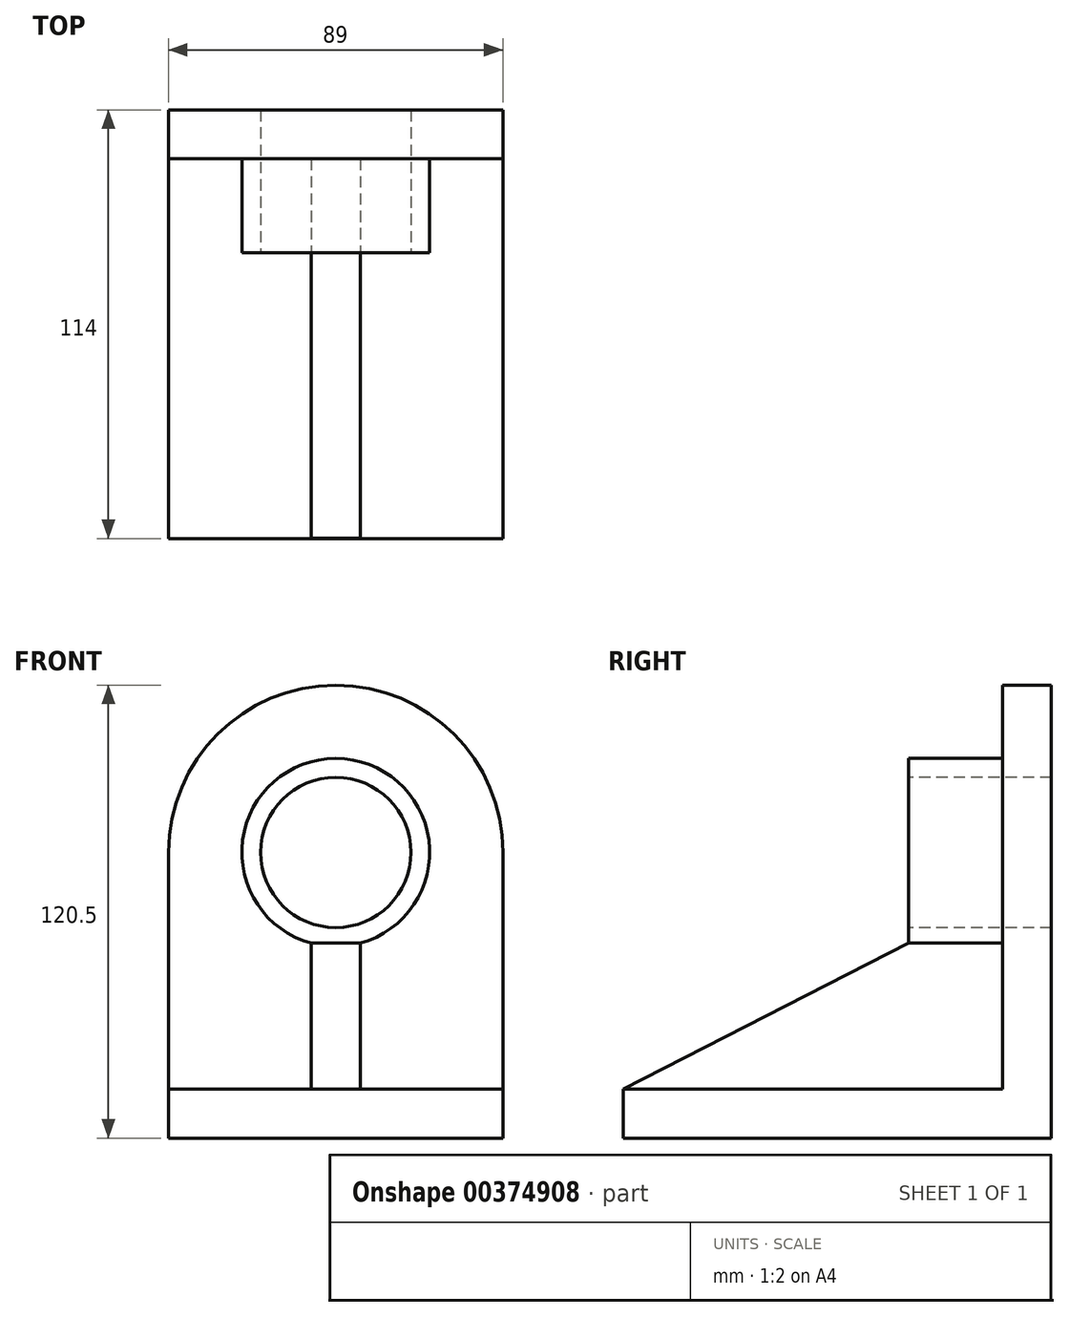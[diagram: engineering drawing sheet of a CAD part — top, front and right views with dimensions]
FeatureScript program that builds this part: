
annotation { "Feature Type Name" : "Feature", "Feature Type Description" : "" }
export const myFeature = defineFeature(function(context is Context, id is Id, definition is map)
    precondition{}
    {
        {
            var Q0;
            Q0=qCreatedBy(makeId("Right.planeOp"),FACE);
            var sketch = newSketch(context, id + "F0", { "sketchPlane" : qUnion([Q0])});
            skLineSegment(sketch, "E0", {"start": v(-64.11, -63.37) * mm, "end": v(49.89, -63.37) * mm});
            skLineSegment(sketch, "E1", {"start": v(49.89, -63.37) * mm, "end": v(49.89, 57.13) * mm});
            skLineSegment(sketch, "E2", {"start": v(49.89, 57.13) * mm, "end": v(36.89, 57.13) * mm});
            skLineSegment(sketch, "E3", {"start": v(36.89, 57.13) * mm, "end": v(36.89, -50.37) * mm});
            skLineSegment(sketch, "E4", {"start": v(36.89, -50.37) * mm, "end": v(-64.11, -50.37) * mm});
            skLineSegment(sketch, "E5", {"start": v(-64.11, -63.37) * mm, "end": v(-64.11, -50.37) * mm});
            skSolve(sketch);
        }
        {
            var Q0;
            Q0=makeQuery(id+"F0.imprint","IMPRINT",FACE,{"disambiguationData":[TD([[makeQuery(id+"F0.imprint","IMPRINT",EDGE,{"derivedFrom":sQuery(id+"F0.wireOp",EDGE,"E0")}),1.0]])]});
            extrude(context, id + "F1", {"entities" : qUnion([Q0]), "depth" : 44.5 * mm, "hasSecondDirection" : true, "secondDirectionOppositeDirection" : true, "secondDirectionDepth" : 44.5 * mm});
        }
        {
            var Q0;
            Q0=makeQuery(id+"F1.opExtrude","SWEPT_FACE",FACE,{"disambiguationData":[OSD([sQuery(id+"F0.wireOp",EDGE,"E3")])]});
            var sketch = newSketch(context, id + "F2", { "sketchPlane" : qUnion([Q0])});
            skArc(sketch, "E6", {"start": v(44.5, 12.63) * mm, "mid": v(0, 57.13) * mm, "end": v(-44.5, 12.63) * mm});
            skLineSegment(sketch, "E7", {"start": v(-44.5, 12.63) * mm, "end": v(-44.5, 57.13) * mm});
            skLineSegment(sketch, "E8", {"start": v(-44.5, 57.13) * mm, "end": v(44.5, 57.13) * mm});
            skLineSegment(sketch, "E9", {"start": v(44.5, 57.13) * mm, "end": v(44.5, 12.63) * mm});
            skCircle(sketch, "E10", {"center": v(0, 12.63) * mm, "radius": 20 * mm});
            skCircle(sketch, "E11.0", {"center": v(0, 12.63) * mm, "radius": 25 * mm});
            skSolve(sketch);
        }
        {
            var Q0;
            {var subQ0=sQuery(id+"F2.wireOp",EDGE,"E9");Q0=makeQuery(id+"F2.imprint","IMPRINT",FACE,{"disambiguationData":[TD([[makeQuery(id+"F2.imprint","IMPRINT",EDGE,{"derivedFrom":subQ0}),-1.0]])]});}
            var Q1;
            {var subQ0=sQuery(id+"F2.wireOp",EDGE,"E7");Q1=makeQuery(id+"F2.imprint","IMPRINT",FACE,{"disambiguationData":[TD([[makeQuery(id+"F2.imprint","IMPRINT",EDGE,{"derivedFrom":subQ0}),1.0]])]});}
            extrude(context, id + "F3", {"entities" : qUnion([Q0, Q1]), "operationType" : NewBodyOperationType.REMOVE, "oppositeDirection" : true, "depth" : 25.4 * mm});
        }
        {
            var Q0;
            Q0=makeQuery(id+"F2.imprint","IMPRINT",FACE,{"disambiguationData":[TD([[makeQuery(id+"F2.imprint","IMPRINT",EDGE,{"derivedFrom":sQuery(id+"F2.wireOp",EDGE,"E10")}),1.0]])]});
            extrude(context, id + "F4", {"entities" : qUnion([Q0]), "operationType" : NewBodyOperationType.REMOVE, "oppositeDirection" : true, "depth" : 25.4 * mm});
        }
        {
            var Q0;
            Q0=makeQuery(id+"F2.imprint","IMPRINT",FACE,{"disambiguationData":[TD([[makeQuery(id+"F2.imprint","IMPRINT",EDGE,{"derivedFrom":sQuery(id+"F2.wireOp",EDGE,"E10")}),-1.0]])]});
            extrude(context, id + "F5", {"entities" : qUnion([Q0]), "operationType" : NewBodyOperationType.ADD, "depth" : 25 * mm});
        }
        {
            var Q0;
            Q0=makeQuery(id+"F5.opExtrude","CAP_FACE",FACE,{"disambiguationData":[OSD([sQuery(id+"F2.wireOp",EDGE,"E10"),sQuery(id+"F2.wireOp",EDGE,"E11.0")])],"isStart":false});
            var sketch = newSketch(context, id + "F6", { "sketchPlane" : qUnion([Q0])});
            skLineSegment(sketch, "E12", {"start": v(0, -7.37) * mm, "end": v(6.5, -7.37) * mm});
            skLineSegment(sketch, "E13", {"start": v(6.5, -7.37) * mm, "end": v(6.5, -50.55) * mm});
            skLineSegment(sketch, "E14", {"start": v(6.5, -50.55) * mm, "end": v(0, -50.55) * mm});
            skLineSegment(sketch, "E15.MirrorCS", {"start": v(0, -7.37) * mm, "end": v(-6.5, -7.37) * mm});
            skLineSegment(sketch, "E16.MirrorCS", {"start": v(-6.5, -7.37) * mm, "end": v(-6.5, -50.55) * mm});
            skLineSegment(sketch, "E17.MirrorCS", {"start": v(-6.5, -50.55) * mm, "end": v(0, -50.55) * mm});
            skSolve(sketch);
        }
        {
            var Q0;
            {var subQ4=sQuery(id+"F6.wireOp",EDGE,"E14");Q0=makeQuery(id+"F6.imprint","IMPRINT",FACE,{"disambiguationData":[TD([[makeQuery(id+"F6.imprint","IMPRINT",EDGE,{"derivedFrom":subQ4}),-1.0]])]});}
            extrude(context, id + "F7", {"entities" : qUnion([Q0]), "operationType" : NewBodyOperationType.ADD, "endBound" : BoundingType.UP_TO_NEXT, "oppositeDirection" : true, "depth" : 25.4 * mm});
        }
        {
            var Q0;
            Q0=makeQuery(id+"F7.opExtrude","SWEPT_FACE",FACE,{"disambiguationData":[OSD([sQuery(id+"F6.wireOp",EDGE,"E13")])]});
            var sketch = newSketch(context, id + "F8", { "sketchPlane" : qUnion([Q0])});
            skLineSegment(sketch, "E18", {"start": v(11.89, -11.51) * mm, "end": v(-64.11, -50.4) * mm});
            skLineSegment(sketch, "E19", {"start": v(-64.11, -50.4) * mm, "end": v(-64.11, -52.38) * mm});
            skLineSegment(sketch, "E20", {"start": v(-64.11, -52.38) * mm, "end": v(11.89, -53.73) * mm});
            skLineSegment(sketch, "E21", {"start": v(11.89, -53.73) * mm, "end": v(11.89, -11.51) * mm});
            skSolve(sketch);
        }
        {
            var Q0;
            {var subQ5=sQuery(id+"F8.wireOp",EDGE,"E18");Q0=makeQuery(id+"F8.imprint","IMPRINT",FACE,{"disambiguationData":[TD([[makeQuery(id+"F8.imprint","IMPRINT",EDGE,{"derivedFrom":subQ5}),1.0]])]});}
            extrude(context, id + "F9", {"entities" : qUnion([Q0]), "operationType" : NewBodyOperationType.ADD, "oppositeDirection" : true, "depth" : 13 * mm});
        }
    });
